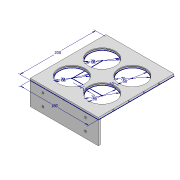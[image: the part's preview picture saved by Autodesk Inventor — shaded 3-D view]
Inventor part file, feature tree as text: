
AUTODESK INVENTOR PART (.ipt)
format: ipt  version: 2020.3 (Build 243373010, 373A)  size: 164,864 bytes
history: native  units: mm
features: sketch x4, extrude x3, hole x2
ambient origin geometry x8: Origin, YZ Plane, XZ Plane, XY Plane, X Axis, Y Axis, Z Axis, Center Point
bodies: Solid1 (feature_tree)
feature tree (9):
  sketch  "Sketch1"  dims[d0=180.0mm d1=200.0mm]
  extrude  "Extrusion1"  Depth=200.0mm
  extrude  "Extrusion2"  Depth=70.0mm
  hole  "Hole1"  [1 undecoded]
  extrude  "Extrusion3"  Depth=5.0mm TaperAngle=0.0deg
  hole  "Hole2"  [1 undecoded]
  sketch  "Sketch2"  dims[d2=70.0mm d3=70.0mm]
  sketch  "Sketch3"  dims[d4=70.0mm d5=70.0mm d6=10.0mm]
  sketch  "Sketch4"  dims[d7=10.0mm d9=5.0mm d10=0.0mm d11=68.0mm d12=68.0mm d13=68.0mm d14=68.0mm d15=3.0mm d16=0.0mm d18=2.0mm d19=2.0mm d20=2.0mm d21=2.0mm d23=40.0mm d24=40.0mm d25=40.0mm d26=40.0mm d28=3.242mm d29=8.0mm d30=3.708mm d31=2.0mm d32=14.3117mm d33=11.8mm d34=0.0mm d35=6.0mm d36=60.0mm d37=0.0mm d38=4.917mm d39=12.0mm d40=3.708mm d41=2.0mm d42=14.3117mm d43=17.1mm d44=0.0mm d45=2.5mm]
note: 2 required parameter values undecoded (feature->parameter linkage not recoverable at this tier; creation-order binding heuristic only, values carry confidence <= 0.55)
